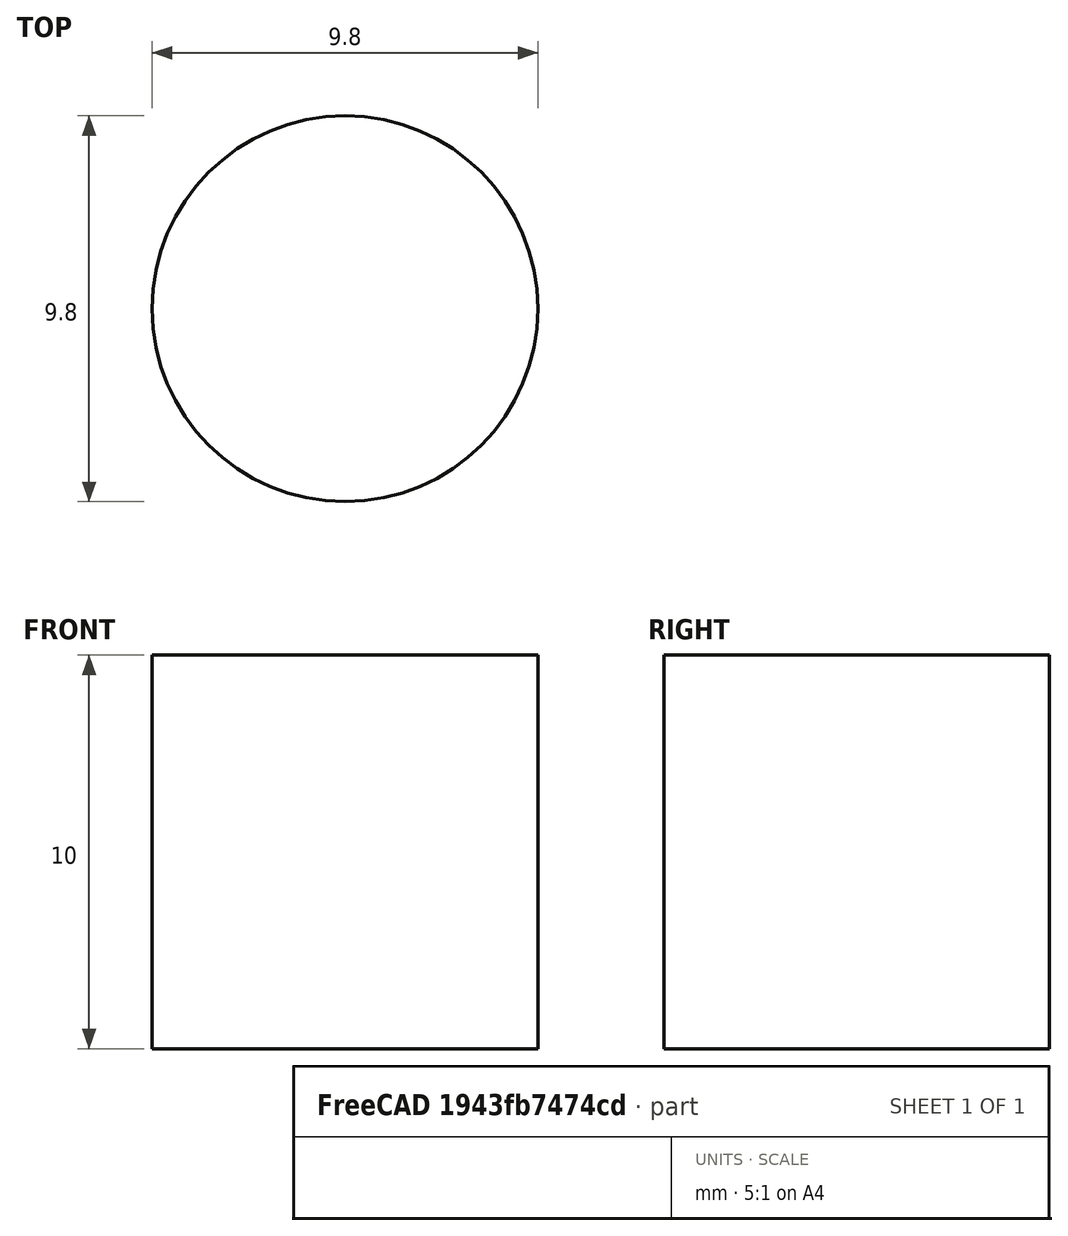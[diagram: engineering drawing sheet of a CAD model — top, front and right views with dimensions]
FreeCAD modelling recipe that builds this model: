
FCSTD DOCUMENT  (FreeCAD 0.21R33771 (Git))
Label: shortFuel
License: All rights reserved
LicenseURL: http://en.wikipedia.org/wiki/All_rights_reserved
objects: Part::FeaturePython×5, App::DocumentObjectGroupPython×2, Sketcher::SketchObject×1, PartDesign::Pad×1, PartDesign::Body×1, App::MaterialObjectPython×1, Fem::FemMeshObject×1
note: 9 computed .brp shape members not serialized (recipe doc carries the construction recipe); baked Part::Feature solids carry a one-line shape summary decoded from their .brp

FEATURE [Sketcher::SketchObject] Sketch
  FullyConstrained = true
  MapMode = 5
  Support = -> [XY_Plane]
  sketch-geometry (1):
    g0: Circle CenterX=0 CenterY=0 CenterZ=0 NormalX=0 NormalY=0 NormalZ=1 AngleXU=0 Radius=4.9
  constraints (2):
    c: Coincident(g0,g-1)
    c: Diameter(g0) = 9.8
FEATURE [PartDesign::Pad] Pad
  Direction = (0,0,1)
  Length = 10
  Length2 = 10
  Profile = -> Sketch
  ReferenceAxis = -> Sketch [N_Axis]
  Type = 0
FEATURE [PartDesign::Body] Body
  Group = -> [Sketch,Pad]
  Origin = -> Origin
  Tip = -> Pad
FEATURE [Part::FeaturePython] PhysicsModel  # WARN: FeaturePython — macro-defined, semantics opaque (R4)
  Flow = 1
  Phase = 0
  SRFModelAxis = (0,0,0)
  SRFModelCoR = (0,0,0)
  SRFModelEnabled = false
  SRFModelRPM = 0
  Time = 0
  Turbulence = 1
  TurbulenceModel = 0
  gx = 0
  gy = 0
  gz = -9800
FEATURE [App::MaterialObjectPython] FluidProperties  label="Air"  # material (typed FeaturePython)
  Category = 1
  Material = CardName=AirCompressible; Cp=1004.703 J/kg/K; Description=Compressible air properties; MolarMass=0.0289643897748887 kg/mol; Name=Air; SutherlandRefTemperature=273.15 K; SutherlandRefViscosity=1.716e-5 kg/m/s; SutherlandTemperature=110.4 K; Type=Compressible
FEATURE [Part::FeaturePython] InitialiseFields  # WARN: FeaturePython — macro-defined, semantics opaque (R4)
  PotentialFlow = false
  PotentialFlowP = false
  Pressure = 100
  ReThetat = 1
  Temperature = 800
  UseInletTemperatureValue = false
  UseInletTurbulenceValues = false
  UseInletUValues = false
  UseOutletPValue = false
  Ux = 0
  Uy = 0
  Uz = 0
  epsilon = 50000000
  gammaInt = 1
  k = 10000
  nuTilda = 55000000
  nut = 50000000
  omega = 1
FEATURE [Part::FeaturePython] CfdSolver  # WARN: FeaturePython — macro-defined, semantics opaque (R4)
  ConvergenceTol = 0.001
  EndTime = 1
  InputCaseName = case
  MaxCFLNumber = 5
  MaxInterfaceCFLNumber = 5
  MaxIterations = 2000
  Parallel = true
  ParallelCores = 4
  PurgeWrite = 0
  StartFrom = 0
  SteadyWriteInterval = 100
  TimeStep = 0.001
  TransientWriteInterval = 0.1
FEATURE [Part::FeaturePython] CfdFluidBoundary001  label="endCaps"  # WARN: FeaturePython — macro-defined, semantics opaque (R4)
  BoundarySubType = 0
  BoundaryType = 0
  DefaultBoundary = false
  DissipationRate = 50000000
  HeatFlux = 0
  HeatTransferCoeff = 0
  Intermittency = 1
  MassFlowRate = 0
  NuTilda = 55000000
  PeriodicCentreOfRotation = (0,0,0)
  PeriodicCentreOfRotationAxis = (0,0,0)
  PeriodicMaster = true
  PeriodicSeparationVector = (0,0,0)
  PorousBaffleMethod = 0
  Pressure = 100
  PressureDropCoeff = 0
  ReThetat = 1
  RelativeToFrame = false
  ReverseNormal = false
  RotationalPeriodic = false
  RoughnessConstant = 0.5
  RoughnessHeight = 0
  ScreenSpacing = 2
  ScreenWireDiameter = 0.2
  ShapeRefs = -> [Pad]
  SlipRatio = 0
  SpecificDissipationRate = 1
  Temperature = 290
  ThermalBoundaryType = 1
  TurbulenceInletSpecification = 1
  TurbulenceIntensityPercentage = 1
  TurbulenceLengthScale = 100
  TurbulentKineticEnergy = 10000
  TurbulentViscosity = 50000000
  Ux = 0
  Uy = 0
  Uz = 0
  VelocityIsCartesian = true
  VelocityMag = 0
  VolFlowRate = 0
  kEqnTurbulentKineticEnergy = 10000
  kEqnTurbulentViscosity = 50000000
FEATURE [Part::FeaturePython] CfdFluidBoundary  label="circularWall"  # WARN: FeaturePython — macro-defined, semantics opaque (R4)
  BoundarySubType = 0
  BoundaryType = 0
  DefaultBoundary = false
  DissipationRate = 50000000
  HeatFlux = 220000
  HeatTransferCoeff = 0
  Intermittency = 1
  MassFlowRate = 0
  NuTilda = 55000000
  PeriodicCentreOfRotation = (0,0,0)
  PeriodicCentreOfRotationAxis = (0,0,0)
  PeriodicMaster = true
  PeriodicSeparationVector = (0,0,0)
  PorousBaffleMethod = 0
  Pressure = 100
  PressureDropCoeff = 0
  ReThetat = 1
  RelativeToFrame = false
  ReverseNormal = false
  RotationalPeriodic = false
  RoughnessConstant = 0.5
  RoughnessHeight = 0
  ScreenSpacing = 2
  ScreenWireDiameter = 0.2
  ShapeRefs = -> [Pad]
  SlipRatio = 0
  SpecificDissipationRate = 1
  Temperature = 290
  ThermalBoundaryType = 2
  TurbulenceInletSpecification = 1
  TurbulenceIntensityPercentage = 1
  TurbulenceLengthScale = 100
  TurbulentKineticEnergy = 10000
  TurbulentViscosity = 50000000
  Ux = 0
  Uy = 0
  Uz = 0
  VelocityIsCartesian = true
  VelocityMag = 0
  VolFlowRate = 0
  kEqnTurbulentKineticEnergy = 10000
  kEqnTurbulentViscosity = 50000000
FEATURE [Fem::FemMeshObject] Pad_MeshSurfaceMesh
FEATURE [App::DocumentObjectGroupPython] Pad_Mesh  # scripted group (container) (typed FeaturePython)
  CaseName = meshCase
  CellsBetweenLevels = 3
  CharacteristicLengthMax = 0.5
  ConvertToDualMesh = false
  EdgeRefinement = 1
  ElementDimension = 1
  Group = -> [Pad_MeshSurfaceMesh]
  ImplicitEdgeDetection = false
  MeshUtility = 0
  NumberOfProcesses = 1
  NumberOfThreads = 0
  Part = -> Pad
  PointInMesh = x=0 m; y=0 m; z=0 m
  STLAngularMeshDensity = 100
  STLRelativeLinearDeflection = 0.001
FEATURE [App::DocumentObjectGroupPython] CfdAnalysis  # scripted group (container) (typed FeaturePython)
  Group = -> [PhysicsModel,FluidProperties,InitialiseFields,CfdSolver,CfdFluidBoundary001,CfdFluidBoundary,Pad_Mesh]
  HostfileName = ../mpi_hostfile
  IsActiveAnalysis = true
  NeedsCaseRewrite = true
  NeedsMeshRerun = false
  NeedsMeshRewrite = true
  UseHostfile = false
